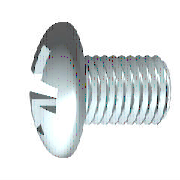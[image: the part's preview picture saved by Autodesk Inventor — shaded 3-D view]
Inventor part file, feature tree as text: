
AUTODESK INVENTOR PART (.ipt)
format: ipt  version: 2018.1 (Build 221171000, 171)  size: 278,016 bytes
history: native  units: mm (DEFAULTED — no unit token found)
features: extrude x1, other x1, plane x1
ambient origin geometry x7: Origin, YZ Plane, XZ Plane, X Axis, Y Axis, Z Axis, Center Point
bodies: Solid1 (feature_tree), Body (feature_tree)
feature tree (3):
  extrude  "Slot"  Depth=2.5mm
  other  "Cut"
  plane  "Work Plane3"
